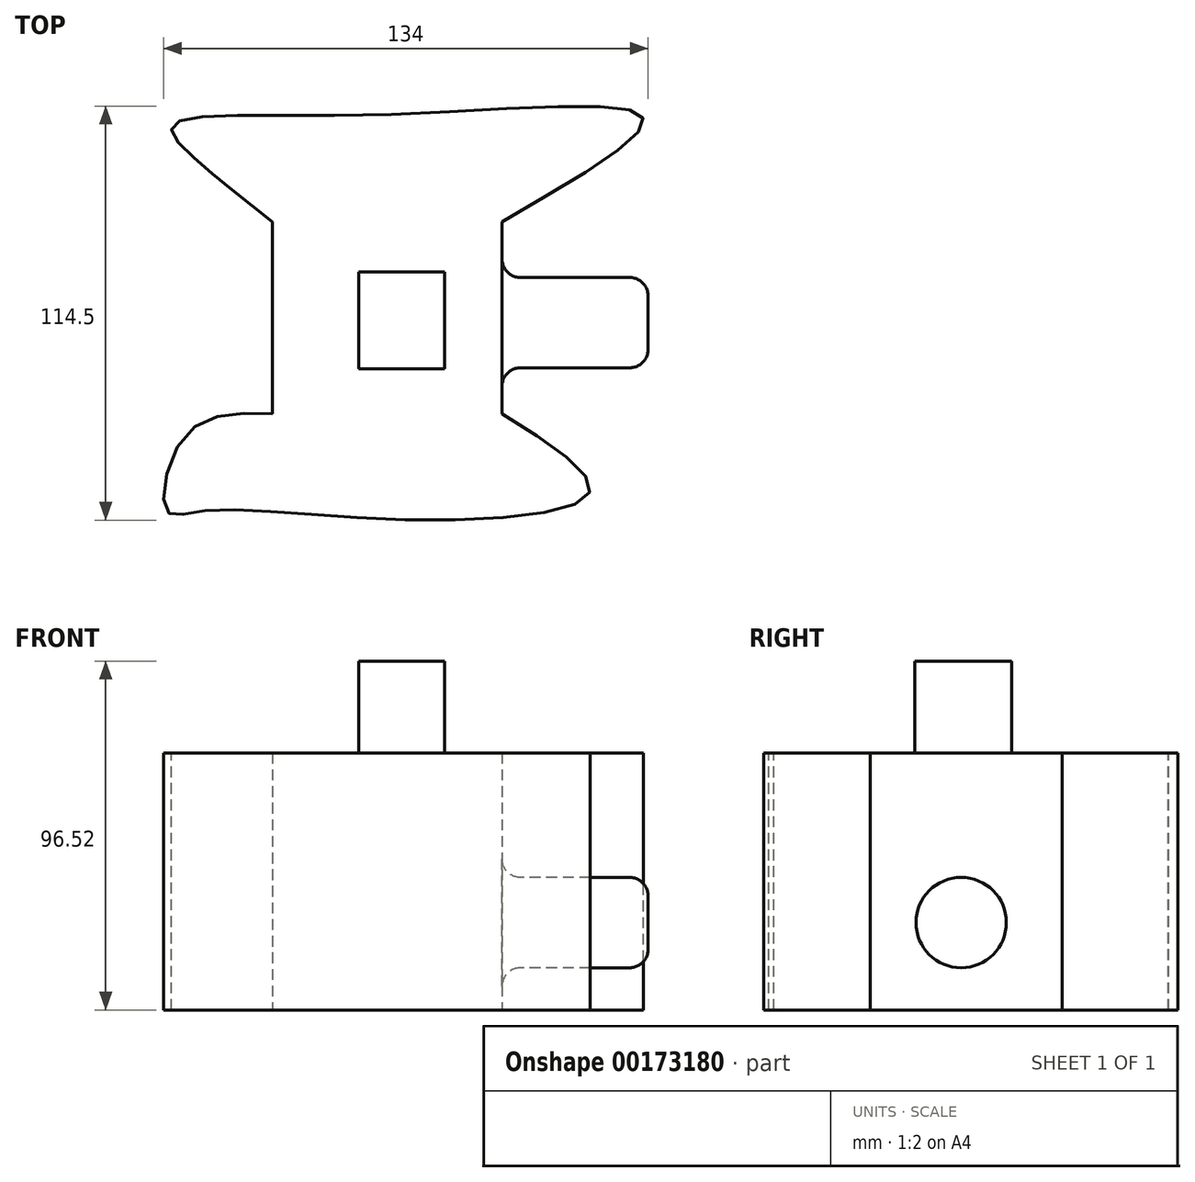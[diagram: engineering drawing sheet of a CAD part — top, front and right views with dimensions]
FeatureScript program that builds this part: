
annotation { "Feature Type Name" : "Feature", "Feature Type Description" : "" }
export const myFeature = defineFeature(function(context is Context, id is Id, definition is map)
    precondition{}
    {
        {
            var Q0;
            Q0=qCreatedBy(makeId("Top.planeOp"),FACE);
            var sketch = newSketch(context, id + "F0", { "sketchPlane" : qUnion([Q0])});
            skLineSegment(sketch, "E0.left", {"start": v(-37.02, 27.91) * mm, "end": v(-37.02, -25.17) * mm});
            skLineSegment(sketch, "E0.right", {"start": v(26.44, 27.91) * mm, "end": v(26.44, -25.17) * mm});
            skFitSpline(sketch, "E1", {"points": [v(26.44, -25.17) * mm, v(50.73, -46.71) * mm, v(1.76, -54.55) * mm, v(-56.8, -52.2) * mm, v(-66.4, -52) * mm, v(-60.91, -30.85) * mm, v(-37.02, -25.17) * mm], "startDerivative": vector(226.39, -142.5) * mm, "endDerivative": vector(182.9, -6.16) * mm});
            skFitSpline(sketch, "E2", {"points": [v(-37.02, 27.91) * mm, v(-57.39, 44.36) * mm, v(-64.83, 54.16) * mm, v(-9.8, 57.49) * mm, v(65.42, 56.7) * mm, v(26.44, 27.91) * mm], "startDerivative": vector(-130.18, 101.74) * mm, "endDerivative": vector(-282.58, -162.68) * mm});
            skSolve(sketch);
        }
        {
            var Q0;
            Q0=makeQuery(id+"F0.imprint","IMPRINT",FACE,{"disambiguationData":[TD([[makeQuery(id+"F0.imprint","IMPRINT",EDGE,{"derivedFrom":sQuery(id+"F0.wireOp",EDGE,"E0.left")}),1.0]])]});
            extrude(context, id + "F1", {"entities" : qUnion([Q0]), "depth" : 45.72 * mm});
        }
        {
            var Q0;
            Q0=makeQuery(id+"F1.opExtrude","SWEPT_FACE",FACE,{"disambiguationData":[OSD([sQuery(id+"F0.wireOp",EDGE,"E0.right")])]});
            var sketch = newSketch(context, id + "F2", { "sketchPlane" : qUnion([Q0])});
            skCircle(sketch, "E3", {"center": v(0, 24.17) * mm, "radius": 12.5 * mm});
            skSolve(sketch);
        }
        {
            var Q0;
            Q0=makeQuery(id+"F2.imprint","IMPRINT",FACE,{"disambiguationData":[TD([[makeQuery(id+"F2.imprint","IMPRINT",EDGE,{"derivedFrom":sQuery(id+"F2.wireOp",EDGE,"E3")}),1.0]])]});
            extrude(context, id + "F3", {"entities" : qUnion([Q0]), "operationType" : NewBodyOperationType.ADD, "depth" : 40.4 * mm});
        }
        {
            var Q0;
            Q0=makeQuery(id+"F3.opExtrude","SWEPT_FACE",FACE,{"disambiguationData":[OSD([sQuery(id+"F2.wireOp",EDGE,"E3")])]});
            fillet(context, id + "F4", {"entities" : qUnion([Q0]), "radius" : 5.08 * mm, "tangentPropagation" : true, "allowEdgeOverflow" : false});
        }
        {
            var Q0;
            Q0=makeQuery(id+"F1.opExtrude","CAP_FACE",FACE,{"disambiguationData":[OSD([sQuery(id+"F0.wireOp",EDGE,"E0.left"),sQuery(id+"F0.wireOp",EDGE,"E0.right"),sQuery(id+"F0.wireOp",EDGE,"E1"),sQuery(id+"F0.wireOp",EDGE,"E2")])],"isStart":false});
            var sketch = newSketch(context, id + "F5", { "sketchPlane" : qUnion([Q0])});
            skLineSegment(sketch, "E4.bottom", {"start": v(-17.63, 24.78) * mm, "end": v(11.36, 24.78) * mm});
            skLineSegment(sketch, "E4.top", {"start": v(-17.63, -18.5) * mm, "end": v(11.36, -18.5) * mm});
            skLineSegment(sketch, "E4.left", {"start": v(-17.63, 24.78) * mm, "end": v(-17.63, -18.5) * mm});
            skLineSegment(sketch, "E4.right", {"start": v(11.36, 24.78) * mm, "end": v(11.36, -18.5) * mm});
            skSolve(sketch);
        }
        {
            var Q0;
            Q0=makeQuery(id+"F5.imprint","IMPRINT",FACE,{"disambiguationData":[TD([[makeQuery(id+"F5.imprint","IMPRINT",EDGE,{"derivedFrom":sQuery(id+"F5.wireOp",EDGE,"E4.bottom")}),-1.0]])]});
            var Q1;
            Q1=makeQuery(id+"F5.imprint","IMPRINT",FACE,{"disambiguationData":[TD([[makeQuery(id+"F5.imprint","IMPRINT",EDGE,{"derivedFrom":sQuery(id+"F5.wireOp",EDGE,"E4.bottom")}),1.0]])]});
            var Q2;
            Q2=makeQuery(id+"F1.opExtrude","CAP_FACE",FACE,{"disambiguationData":[OSD([sQuery(id+"F0.wireOp",EDGE,"E0.left"),sQuery(id+"F0.wireOp",EDGE,"E0.right"),sQuery(id+"F0.wireOp",EDGE,"E1"),sQuery(id+"F0.wireOp",EDGE,"E2")])],"isStart":false});
            var Q3;
            Q3=makeQuery(id+"F1.opExtrude","CAP_FACE",FACE,{"disambiguationData":[OSD([sQuery(id+"F0.wireOp",EDGE,"E0.left"),sQuery(id+"F0.wireOp",EDGE,"E0.right"),sQuery(id+"F0.wireOp",EDGE,"E1"),sQuery(id+"F0.wireOp",EDGE,"E2")])],"isStart":true});
            extrude(context, id + "F6", {"entities" : qUnion([Q0, Q1, Q2, Q3]), "operationType" : NewBodyOperationType.ADD, "depth" : 25.4 * mm});
        }
        {
            var Q0;
            {var subQ0=sQuery(id+"F0.wireOp",EDGE,"E2");var subQ1=sQuery(id+"F0.wireOp",EDGE,"E1");var subQ2=sQuery(id+"F0.wireOp",EDGE,"E0.right");var subQ3=sQuery(id+"F0.wireOp",EDGE,"E0.left");Q0=makeQuery(id+"F6.opExtrude","CAP_FACE",FACE,{"disambiguationData":[OSD([subQ3,subQ2,subQ1,subQ0]),TDD([makeQuery(id+"F1.opExtrude","CAP_FACE",FACE,{"disambiguationData":[OSD([subQ3,subQ2,subQ1,subQ0])],"isStart":false})])],"isStart":false});}
            var sketch = newSketch(context, id + "F7", { "sketchPlane" : qUnion([Q0])});
            skLineSegment(sketch, "E5.bottom", {"start": v(-13.12, 14) * mm, "end": v(10.58, 14) * mm});
            skLineSegment(sketch, "E5.top", {"start": v(-13.12, -12.83) * mm, "end": v(10.58, -12.83) * mm});
            skLineSegment(sketch, "E5.left", {"start": v(-13.12, 14) * mm, "end": v(-13.12, -12.83) * mm});
            skLineSegment(sketch, "E5.right", {"start": v(10.58, 14) * mm, "end": v(10.58, -12.83) * mm});
            skSolve(sketch);
        }
        {
            var Q0;
            Q0=makeQuery(id+"F7.imprint","IMPRINT",FACE,{"disambiguationData":[TD([[makeQuery(id+"F7.imprint","IMPRINT",EDGE,{"derivedFrom":sQuery(id+"F7.wireOp",EDGE,"E5.bottom")}),-1.0]])]});
            extrude(context, id + "F8", {"entities" : qUnion([Q0]), "operationType" : NewBodyOperationType.ADD, "depth" : 25.4 * mm});
        }
    });
